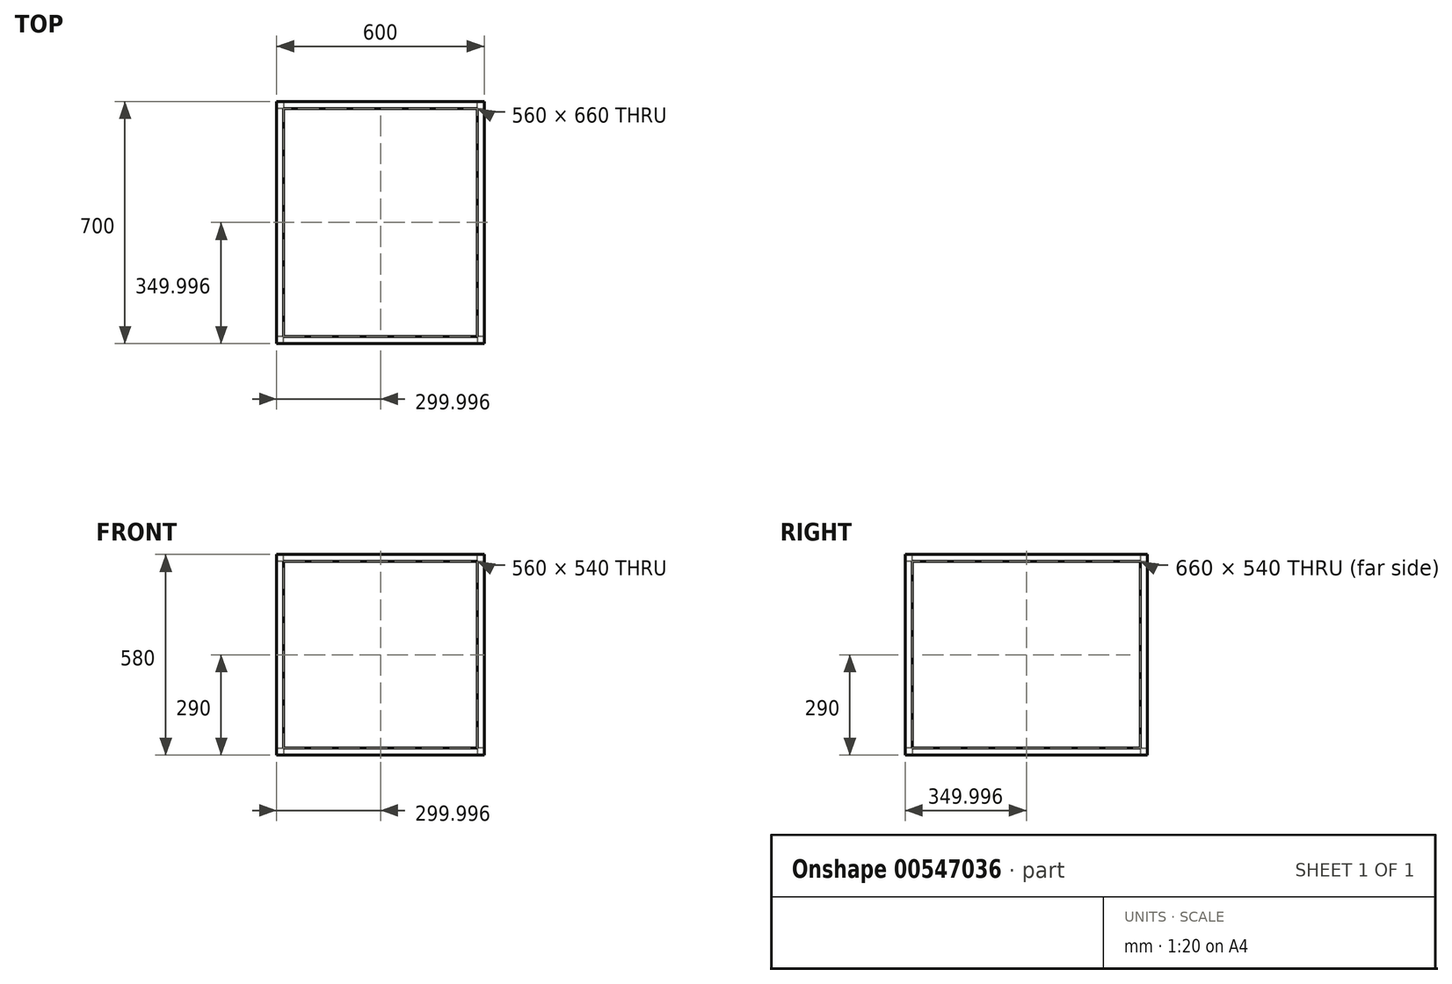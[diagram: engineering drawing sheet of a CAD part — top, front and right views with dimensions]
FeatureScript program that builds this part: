
annotation { "Feature Type Name" : "Feature", "Feature Type Description" : "" }
export const myFeature = defineFeature(function(context is Context, id is Id, definition is map)
    precondition{}
    {
        {
            var Q0;
            Q0=qCreatedBy(makeId("Top.planeOp"),FACE);
            var sketch = newSketch(context, id + "F0", { "sketchPlane" : qUnion([Q0])});
            skLineSegment(sketch, "E0.bottom", {"start": v(-349.06, 480.52) * mm, "end": v(250.94, 480.52) * mm});
            skLineSegment(sketch, "E0.top", {"start": v(-349.06, -219.48) * mm, "end": v(250.94, -219.48) * mm});
            skLineSegment(sketch, "E0.left", {"start": v(-349.06, 480.52) * mm, "end": v(-349.06, -219.48) * mm});
            skLineSegment(sketch, "E0.right", {"start": v(250.94, 480.52) * mm, "end": v(250.94, -219.48) * mm});
            skLineSegment(sketch, "E1.bottom", {"start": v(-329.06, -199.48) * mm, "end": v(230.94, -199.48) * mm});
            skLineSegment(sketch, "E1.top", {"start": v(-329.06, 460.52) * mm, "end": v(230.94, 460.52) * mm});
            skLineSegment(sketch, "E1.left", {"start": v(-329.06, -199.48) * mm, "end": v(-329.06, 460.52) * mm});
            skLineSegment(sketch, "E1.right", {"start": v(230.94, -199.48) * mm, "end": v(230.94, 460.52) * mm});
            skLineSegment(sketch, "E2", {"start": v(-329.06, 460.52) * mm, "end": v(-349.06, 460.52) * mm});
            skLineSegment(sketch, "E3", {"start": v(-329.06, 460.52) * mm, "end": v(-329.06, 480.52) * mm});
            skLineSegment(sketch, "E4", {"start": v(-329.06, -199.48) * mm, "end": v(-329.06, -219.48) * mm});
            skLineSegment(sketch, "E5", {"start": v(-329.06, -199.48) * mm, "end": v(-349.06, -199.48) * mm});
            skSolve(sketch);
        }
        {
            var Q0;
            {var subQ0=sQuery(id+"F0.wireOp",EDGE,"E0.right");Q0=makeQuery(id+"F0.imprint","IMPRINT",FACE,{"disambiguationData":[TD([[makeQuery(id+"F0.imprint","IMPRINT",EDGE,{"derivedFrom":subQ0}),-1.0]])]});}
            var Q1;
            Q1=makeQuery(id+"F0.imprint","IMPRINT",FACE,{"disambiguationData":[TD([[makeQuery(id+"F0.imprint","IMPRINT",EDGE,{"derivedFrom":sQuery(id+"F0.wireOp",EDGE,"E1.left")}),1.0]])]});
            var Q2;
            {var subQ4=sQuery(id+"F0.wireOp",EDGE,"E2");Q2=makeQuery(id+"F0.imprint","IMPRINT",FACE,{"disambiguationData":[TD([[makeQuery(id+"F0.imprint","IMPRINT",EDGE,{"derivedFrom":subQ4}),-1.0]])]});}
            var Q3;
            {var subQ3=sQuery(id+"F0.wireOp",EDGE,"E4");Q3=makeQuery(id+"F0.imprint","IMPRINT",FACE,{"disambiguationData":[TD([[makeQuery(id+"F0.imprint","IMPRINT",EDGE,{"derivedFrom":subQ3}),-1.0]])]});}
            extrude(context, id + "F1", {"entities" : qUnion([Q0, Q1, Q2, Q3]), "depth" : 20 * mm, "offsetDistance" : 25 * mm});
        }
        {
            var Q0;
            {var subQ4=sQuery(id+"F0.wireOp",EDGE,"E2");Q0=makeQuery(id+"F0.imprint","IMPRINT",FACE,{"disambiguationData":[TD([[makeQuery(id+"F0.imprint","IMPRINT",EDGE,{"derivedFrom":subQ4}),-1.0]])]});}
            var Q1;
            {var subQ3=sQuery(id+"F0.wireOp",EDGE,"E4");Q1=makeQuery(id+"F0.imprint","IMPRINT",FACE,{"disambiguationData":[TD([[makeQuery(id+"F0.imprint","IMPRINT",EDGE,{"derivedFrom":subQ3}),-1.0]])]});}
            extrude(context, id + "F2", {"entities" : qUnion([Q0, Q1]), "operationType" : NewBodyOperationType.ADD, "depth" : 580 * mm, "offsetDistance" : 25 * mm});
        }
        {
            var Q0;
            Q0=makeQuery(id+"F2.opExtrude","SWEPT_FACE",FACE,{"disambiguationData":[OSD([sQuery(id+"F0.wireOp",EDGE,"E5")])]});
            var sketch = newSketch(context, id + "F3", { "sketchPlane" : qUnion([Q0])});
            skLineSegment(sketch, "E6", {"start": v(329.06, 560) * mm, "end": v(349.06, 560) * mm});
            skSolve(sketch);
        }
        {
            var Q0;
            {var subQ0=sQuery(id+"F3.wireOp",EDGE,"E6");Q0=makeQuery(id+"F3.imprint","IMPRINT",FACE,{"disambiguationData":[TD([[makeQuery(id+"F3.imprint","IMPRINT",EDGE,{"derivedFrom":subQ0}),1.0]])]});}
            extrude(context, id + "F4", {"entities" : qUnion([Q0]), "operationType" : NewBodyOperationType.ADD, "depth" : 660 * mm, "offsetDistance" : 25 * mm});
        }
        {
            var Q0;
            {var subQ0=sQuery(id+"F0.wireOp",EDGE,"E4");Q0=makeQuery(id+"F4.boolean.opBoolean","MERGE",FACE,{"derivedFrom":[makeQuery(id+"F2.opExtrude","SWEPT_FACE",FACE,{"disambiguationData":[OSD([sQuery(id+"F0.wireOp",EDGE,"E3")])]}),makeQuery(id+"F2.opExtrude","SWEPT_FACE",FACE,{"disambiguationData":[OSD([subQ0])]}),makeQuery(id+"F4.opExtrude","SWEPT_FACE",FACE,{"disambiguationData":[OSD([sQuery(id+"F0.wireOp",EDGE,"E1.bottom"),sQuery(id+"F0.wireOp",EDGE,"E1.left"),subQ0,sQuery(id+"F0.wireOp",EDGE,"E5")])]})]});}
            var sketch = newSketch(context, id + "F5", { "sketchPlane" : qUnion([Q0])});
            skLineSegment(sketch, "E7", {"start": v(-199.48, 560) * mm, "end": v(-219.48, 560) * mm});
            skLineSegment(sketch, "E8", {"start": v(-199.48, 560) * mm, "end": v(-199.48, 580) * mm});
            skLineSegment(sketch, "E9", {"start": v(460.52, 560) * mm, "end": v(480.52, 560) * mm});
            skLineSegment(sketch, "E10", {"start": v(460.52, 580) * mm, "end": v(460.52, 560) * mm});
            skSolve(sketch);
        }
        {
            var Q0;
            {var subQ0=sQuery(id+"F5.wireOp",EDGE,"E7");Q0=makeQuery(id+"F5.imprint","IMPRINT",FACE,{"disambiguationData":[TD([[makeQuery(id+"F5.imprint","IMPRINT",EDGE,{"derivedFrom":subQ0}),-1.0]])]});}
            var Q1;
            {var subQ0=sQuery(id+"F5.wireOp",EDGE,"E9");Q1=makeQuery(id+"F5.imprint","IMPRINT",FACE,{"disambiguationData":[TD([[makeQuery(id+"F5.imprint","IMPRINT",EDGE,{"derivedFrom":subQ0}),1.0]])]});}
            extrude(context, id + "F6", {"entities" : qUnion([Q0, Q1]), "operationType" : NewBodyOperationType.ADD, "depth" : 560 * mm, "offsetDistance" : 25 * mm});
        }
        {
            var Q0;
            {var subQ0=sQuery(id+"F0.wireOp",EDGE,"E0.bottom");var subQ1=sQuery(id+"F0.wireOp",EDGE,"E1.right");var subQ2=sQuery(id+"F0.wireOp",EDGE,"E1.left");var subQ3=sQuery(id+"F0.wireOp",EDGE,"E0.top");var subQ4=sQuery(id+"F0.wireOp",EDGE,"E1.top");var subQ5=sQuery(id+"F0.wireOp",EDGE,"E1.bottom");var subQ6=sQuery(id+"F0.wireOp",EDGE,"E0.right");var subQ7=makeQuery(id+"F1.opExtrude","CAP_FACE",FACE,{"disambiguationData":[OSD([subQ0,subQ3,sQuery(id+"F0.wireOp",EDGE,"E0.left"),subQ6,subQ5,subQ4,subQ2,subQ1])],"isStart":false});Q0=makeQuery(id+"F2.boolean.opBoolean","SPLIT",FACE,{"disambiguationData":[TD([makeQuery(id+"F1.opExtrude","SWEPT_FACE",FACE,{"disambiguationData":[OSD([subQ0])]})])],"derivedFrom":subQ7});}
            var sketch = newSketch(context, id + "F7", { "sketchPlane" : qUnion([Q0])});
            skLineSegment(sketch, "E11", {"start": v(250.94, 460.52) * mm, "end": v(230.94, 460.52) * mm});
            skLineSegment(sketch, "E12", {"start": v(230.94, 460.52) * mm, "end": v(230.94, 480.52) * mm});
            skLineSegment(sketch, "E13", {"start": v(250.94, -199.48) * mm, "end": v(230.94, -199.48) * mm});
            skLineSegment(sketch, "E14", {"start": v(230.94, -199.48) * mm, "end": v(230.94, -219.48) * mm});
            skSolve(sketch);
        }
        {
            var Q0;
            {var subQ0=sQuery(id+"F7.wireOp",EDGE,"E11");Q0=makeQuery(id+"F7.imprint","IMPRINT",FACE,{"disambiguationData":[TD([[makeQuery(id+"F7.imprint","IMPRINT",EDGE,{"derivedFrom":subQ0}),-1.0]])]});}
            var Q1;
            {var subQ0=sQuery(id+"F7.wireOp",EDGE,"E13");Q1=makeQuery(id+"F7.imprint","IMPRINT",FACE,{"disambiguationData":[TD([[makeQuery(id+"F7.imprint","IMPRINT",EDGE,{"derivedFrom":subQ0}),1.0]])]});}
            extrude(context, id + "F8", {"entities" : qUnion([Q0, Q1]), "operationType" : NewBodyOperationType.ADD, "depth" : 560 * mm, "offsetDistance" : 25 * mm});
        }
        {
            var Q0;
            Q0=makeQuery(id+"F8.boolean.opBoolean","MERGE",FACE,{"derivedFrom":[makeQuery(id+"F6.opExtrude","SWEPT_FACE",FACE,{"disambiguationData":[OSD([sQuery(id+"F5.wireOp",EDGE,"E10")])]}),makeQuery(id+"F8.opExtrude","SWEPT_FACE",FACE,{"disambiguationData":[OSD([sQuery(id+"F7.wireOp",EDGE,"E11")])]})]});
            var sketch = newSketch(context, id + "F9", { "sketchPlane" : qUnion([Q0])});
            skLineSegment(sketch, "E15", {"start": v(230.94, 560) * mm, "end": v(230.94, 580) * mm});
            skLineSegment(sketch, "E16", {"start": v(230.94, 560) * mm, "end": v(250.94, 560) * mm});
            skSolve(sketch);
        }
        {
            var Q0;
            {var subQ0=sQuery(id+"F9.wireOp",EDGE,"lIVUudBl-UMOf-0kbQ-xYpW-D7rPUHpAwP2V");Q0=makeQuery(id+"F9.imprint","IMPRINT",FACE,{"disambiguationData":[TD([[makeQuery(id+"F9.imprint","IMPRINT",EDGE,{"derivedFrom":subQ0}),-1.0]])]});}
            var Q1;
            {var subQ0=sQuery(id+"F9.wireOp",EDGE,"E15");Q1=makeQuery(id+"F9.imprint","IMPRINT",FACE,{"disambiguationData":[TD([[makeQuery(id+"F9.imprint","IMPRINT",EDGE,{"derivedFrom":subQ0}),-1.0]])]});}
            extrude(context, id + "F10", {"entities" : qUnion([Q0, Q1]), "operationType" : NewBodyOperationType.ADD, "depth" : 660 * mm, "offsetDistance" : 25 * mm});
        }
    });
